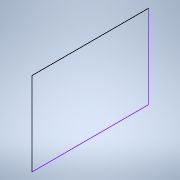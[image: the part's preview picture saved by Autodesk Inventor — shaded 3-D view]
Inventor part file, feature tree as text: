
AUTODESK INVENTOR PART (.ipt)
format: ipt  version: 2020.3 (Build 243373000, 373)  size: 140,800 bytes
history: native  units: mm
features: sketch x5, extrude x3, other x1, fillet x1, hole x1
ambient origin geometry x8: Origin, YZ Plane, XZ Plane, XY Plane, X Axis, Y Axis, Z Axis, Center Point
bodies: Body1 (feature_tree)
feature tree (11):
  other  "ソリッド1"
  extrude  "押し出し1"  Depth=110.0mm
  fillet  "フィレット1"  Radius=116.0mm
  hole  "穴1"  [1 undecoded]
  extrude  "押し出し2"  Depth=5.0mm
  sketch  "スケッチ4"
  sketch  "スケッチ5"
  extrude  "押し出し3"  Depth=101.0mm
  sketch  "スケッチ1"
  sketch  "スケッチ2"
  sketch  "スケッチ3"
note: 1 required parameter value undecoded (feature->parameter linkage not recoverable at this tier; creation-order binding heuristic only, values carry confidence <= 0.55)
